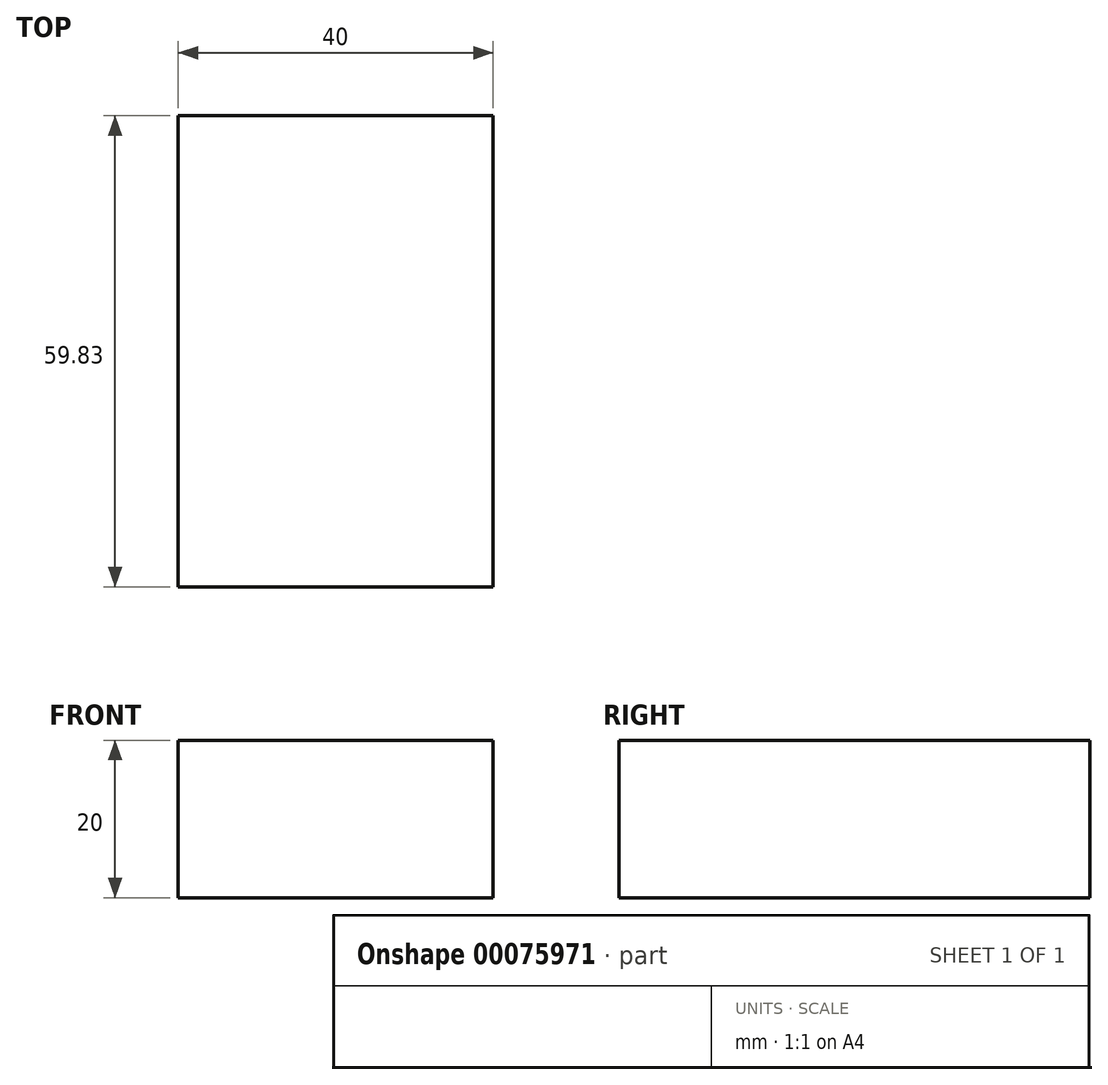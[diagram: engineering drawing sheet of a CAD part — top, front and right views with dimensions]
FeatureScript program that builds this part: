
annotation { "Feature Type Name" : "Feature", "Feature Type Description" : "" }
export const myFeature = defineFeature(function(context is Context, id is Id, definition is map)
    precondition{}
    {
        {
            var Q0;
            Q0=qCreatedBy(makeId("Front.planeOp"),FACE);
            var sketch = newSketch(context, id + "F0", { "sketchPlane" : qUnion([Q0])});
            skLineSegment(sketch, "E0.bottom", {"start": v(-40, 20) * mm, "end": v(0, 20) * mm});
            skLineSegment(sketch, "E0.top", {"start": v(-40, 0) * mm, "end": v(0, 0) * mm});
            skLineSegment(sketch, "E0.left", {"start": v(-40, 20) * mm, "end": v(-40, 0) * mm});
            skLineSegment(sketch, "E0.right", {"start": v(0, 20) * mm, "end": v(0, 0) * mm});
            skSolve(sketch);
        }
        {
            var Q0;
            Q0=qSketchRegion(id+"F0",true);
            var Q1;
            Q1=makeQuery(id+"F0.imprint","IMPRINT",FACE,{"disambiguationData":[TD([[makeQuery(id+"F0.imprint","IMPRINT",EDGE,{"derivedFrom":sQuery(id+"F0.wireOp",EDGE,"E0.bottom")}),-1.0]])]});
            extrude(context, id + "F1", {"entities" : qUnion([Q0, Q1]), "depth" : 59.83 * mm});
        }
    });
